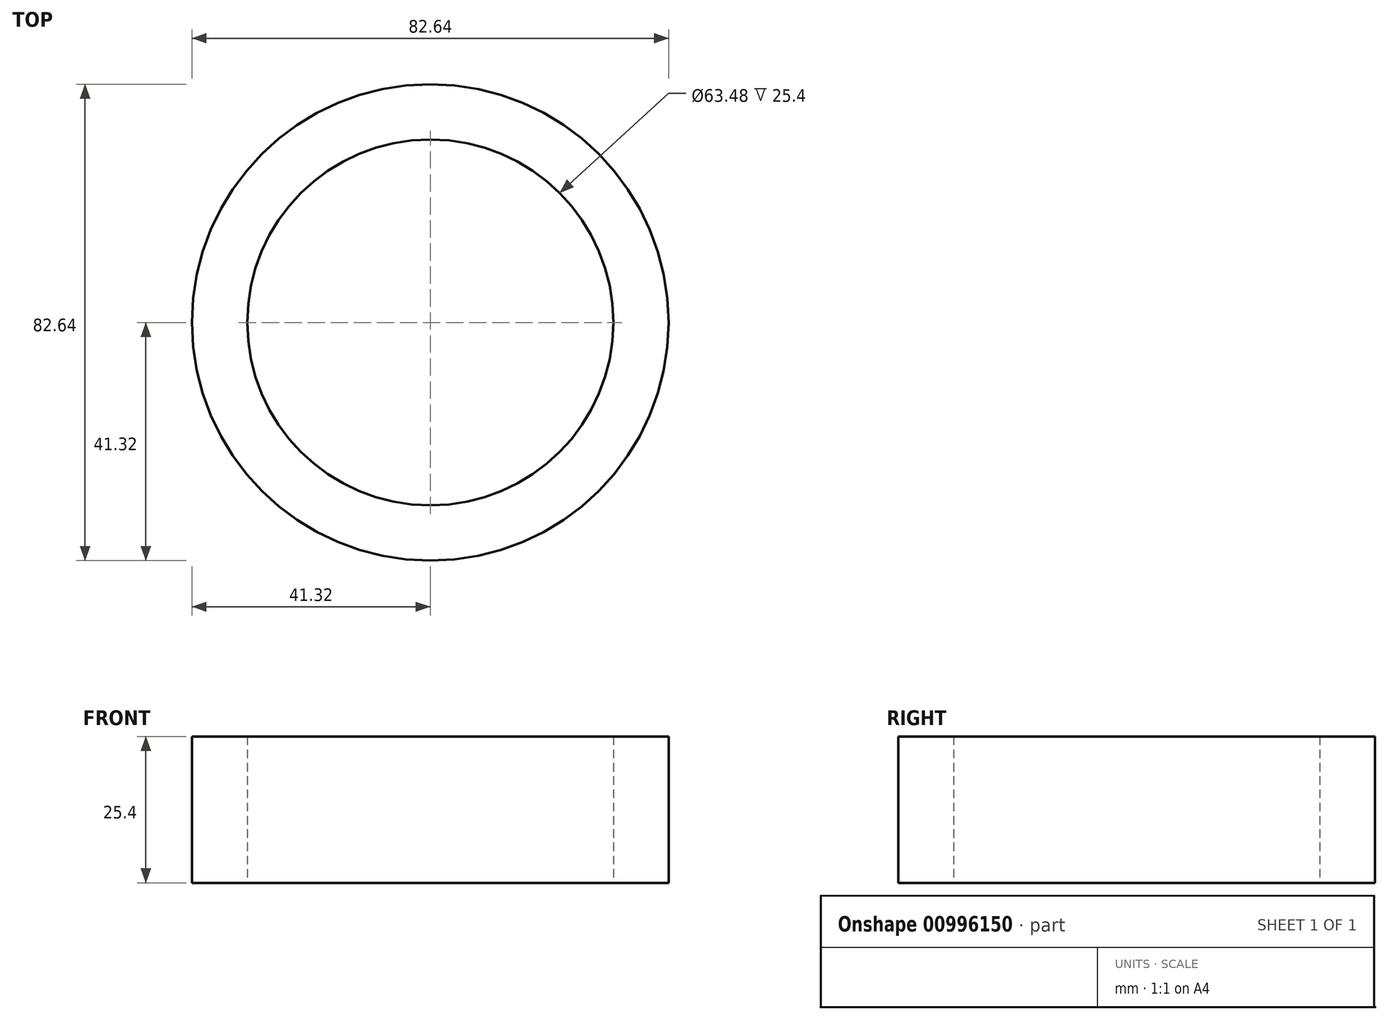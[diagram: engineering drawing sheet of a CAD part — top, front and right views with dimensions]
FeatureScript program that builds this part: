
annotation { "Feature Type Name" : "Feature", "Feature Type Description" : "" }
export const myFeature = defineFeature(function(context is Context, id is Id, definition is map)
    precondition{}
    {
        {
            var Q0;
            Q0=qCreatedBy(makeId("Top.planeOp"),FACE);
            var sketch = newSketch(context, id + "F0", { "sketchPlane" : qUnion([Q0])});
            skCircle(sketch, "E0", {"center": v(0, 0) * mm, "radius": 41.32 * mm});
            skCircle(sketch, "E1", {"center": v(0, 0) * mm, "radius": 31.74 * mm});
            skSolve(sketch);
        }
        {
            var Q0;
            Q0 = qSketchRegion(id + "F0", true);
            extrude(context, id + "F1", {"entities" : qUnion([Q0]), "depth" : 25.4 * mm, "offsetDistance" : 25.4 * mm});
        }
    });
